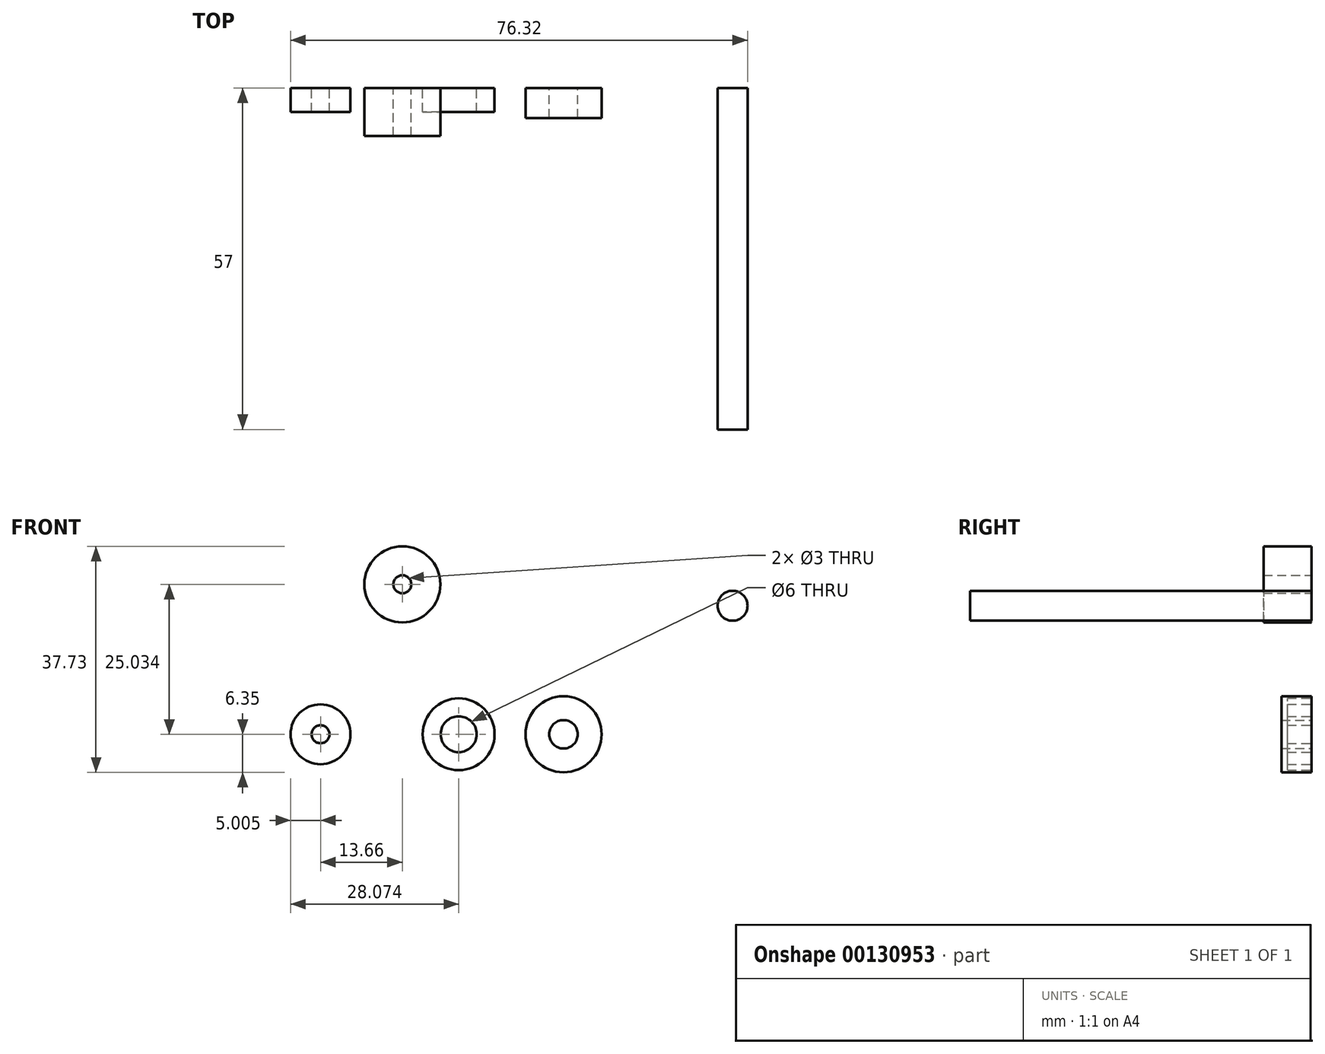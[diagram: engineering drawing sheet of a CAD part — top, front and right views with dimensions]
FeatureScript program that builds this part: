
annotation { "Feature Type Name" : "Feature", "Feature Type Description" : "" }
export const myFeature = defineFeature(function(context is Context, id is Id, definition is map)
    precondition{}
    {
        {
            var Q0;
            Q0=qCreatedBy(makeId("Front.planeOp"),FACE);
            var sketch = newSketch(context, id + "F0", { "sketchPlane" : qUnion([Q0])});
            skCircle(sketch, "E0", {"center": v(0, 0) * mm, "radius": 2.38 * mm});
            skCircle(sketch, "E1", {"center": v(0, 0) * mm, "radius": 6.35 * mm});
            skSolve(sketch);
        }
        {
            var Q0;
            Q0=qSketchRegion(id+"F0",true);
            extrude(context, id + "F1", {"entities" : qUnion([Q0]), "depth" : 5 * mm});
        }
        {
            var Q0;
            Q0=qCreatedBy(makeId("Front.planeOp"),FACE);
            var sketch = newSketch(context, id + "F2", { "sketchPlane" : qUnion([Q0])});
            skCircle(sketch, "E2", {"center": v(28.24, 21.45) * mm, "radius": 2.5 * mm});
            skSolve(sketch);
        }
        {
            var Q0;
            Q0=qSketchRegion(id+"F2",true);
            extrude(context, id + "F3", {"entities" : qUnion([Q0]), "depth" : 57 * mm});
        }
        {
            var Q0;
            Q0=qCreatedBy(makeId("Front.planeOp"),FACE);
            var sketch = newSketch(context, id + "F4", { "sketchPlane" : qUnion([Q0])});
            skCircle(sketch, "E3", {"center": v(-40.58, 0) * mm, "radius": 1.5 * mm});
            skCircle(sketch, "E4", {"center": v(-40.58, 0) * mm, "radius": 5 * mm});
            skSolve(sketch);
        }
        {
            var Q0;
            Q0=qSketchRegion(id+"F4",true);
            extrude(context, id + "F5", {"entities" : qUnion([Q0]), "depth" : 4 * mm});
        }
        {
            var Q0;
            Q0=qCreatedBy(makeId("Front.planeOp"),FACE);
            var sketch = newSketch(context, id + "F6", { "sketchPlane" : qUnion([Q0])});
            skCircle(sketch, "E5", {"center": v(-17.5, 0) * mm, "radius": 3 * mm});
            skCircle(sketch, "E6", {"center": v(-17.5, 0) * mm, "radius": 6 * mm});
            skSolve(sketch);
        }
        {
            var Q0;
            Q0=qSketchRegion(id+"F6",true);
            extrude(context, id + "F7", {"entities" : qUnion([Q0]), "depth" : 4 * mm});
        }
        {
            var Q0;
            Q0=qCreatedBy(makeId("Front.planeOp"),FACE);
            var sketch = newSketch(context, id + "F8", { "sketchPlane" : qUnion([Q0])});
            skCircle(sketch, "E7", {"center": v(-26.92, 25.03) * mm, "radius": 6.35 * mm});
            skCircle(sketch, "E8", {"center": v(-26.92, 25.03) * mm, "radius": 1.5 * mm});
            skSolve(sketch);
        }
        {
            var Q0;
            Q0=qSketchRegion(id+"F8",true);
            extrude(context, id + "F9", {"entities" : qUnion([Q0]), "depth" : 8 * mm});
        }
    });
